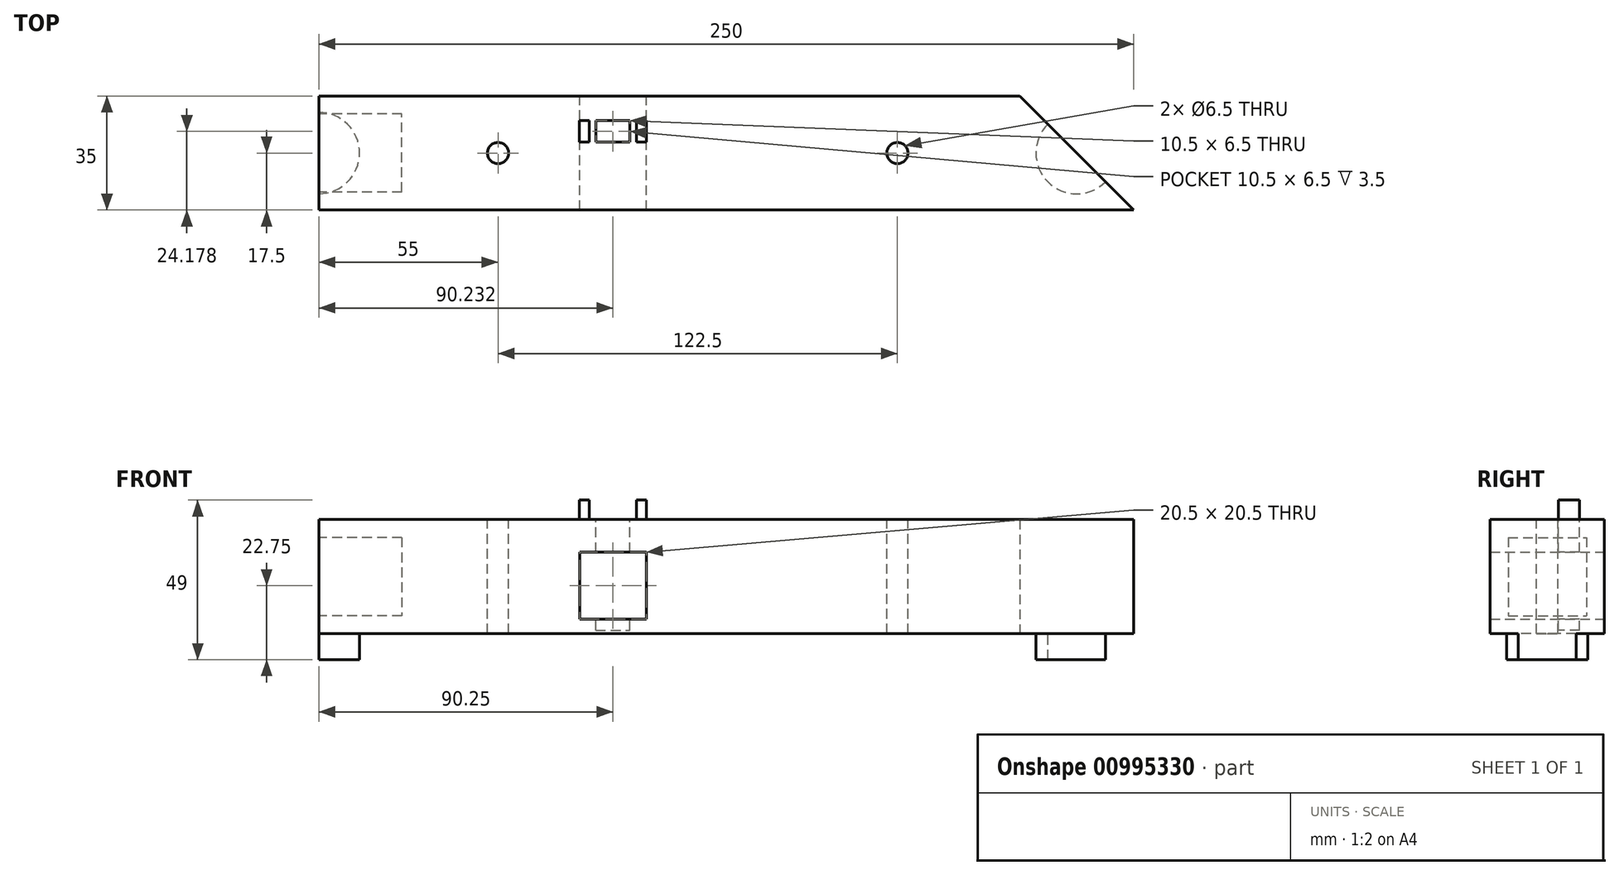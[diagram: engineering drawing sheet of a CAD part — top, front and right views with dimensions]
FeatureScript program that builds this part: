
annotation { "Feature Type Name" : "Feature", "Feature Type Description" : "" }
export const myFeature = defineFeature(function(context is Context, id is Id, definition is map)
    precondition{}
    {
        {
            var Q0;
            Q0=qCreatedBy(makeId("Top.planeOp"),FACE);
            var sketch = newSketch(context, id + "F0", { "sketchPlane" : qUnion([Q0])});
            skLineSegment(sketch, "E0.bottom", {"start": v(125, -17.5) * mm, "end": v(-125, -17.5) * mm});
            skLineSegment(sketch, "E0.top", {"start": v(90, 17.5) * mm, "end": v(-125, 17.5) * mm});
            skLineSegment(sketch, "E0.right", {"start": v(-125, -17.5) * mm, "end": v(-125, 17.5) * mm});
            skPoint(sketch, "E0.middle", {"position": v(0, 0) * mm});
            skPoint(sketch, "E1", {"position": v(90, 17.5) * mm});
            skLineSegment(sketch, "E2", {"start": v(125, -17.5) * mm, "end": v(90, 17.5) * mm});
            skPoint(sketch, "E0.left.end.orphan", {"position": v(125, 17.5) * mm});
            skSolve(sketch);
        }
        {
            var Q0;
            Q0=makeQuery(id+"F0.imprint","IMPRINT",FACE,{"disambiguationData":[TD([[makeQuery(id+"F0.imprint","IMPRINT",EDGE,{"derivedFrom":sQuery(id+"F0.wireOp",EDGE,"E0.bottom")}),-1.0]])]});
            extrude(context, id + "F1", {"entities" : qUnion([Q0]), "depth" : 35 * mm, "offsetDistance" : 25 * mm});
        }
        {
            var Q0;
            Q0=makeQuery(id+"F1.opExtrude","SWEPT_FACE",FACE,{"disambiguationData":[OSD([sQuery(id+"F0.wireOp",EDGE,"E0.right")])]});
            var sketch = newSketch(context, id + "F2", { "sketchPlane" : qUnion([Q0])});
            skLineSegment(sketch, "E3.0", {"start": v(-12, 29.5) * mm, "end": v(-12, 5.5) * mm});
            skLineSegment(sketch, "E3.1", {"start": v(12, 29.5) * mm, "end": v(-12, 29.5) * mm});
            skLineSegment(sketch, "E4.0", {"start": v(12, 5.5) * mm, "end": v(-12, 5.5) * mm});
            skLineSegment(sketch, "E4.1", {"start": v(12, 29.5) * mm, "end": v(12, 5.5) * mm});
            skSolve(sketch);
        }
        {
            var Q0;
            Q0=makeQuery(id+"F2.imprint","IMPRINT",FACE,{"disambiguationData":[TD([[makeQuery(id+"F2.imprint","IMPRINT",EDGE,{"derivedFrom":sQuery(id+"F2.wireOp",EDGE,"E3.0")}),1.0]])]});
            extrude(context, id + "F3", {"entities" : qUnion([Q0]), "operationType" : NewBodyOperationType.REMOVE, "oppositeDirection" : true, "depth" : 25.5 * mm, "offsetDistance" : 25 * mm});
        }
        {
            var Q0;
            Q0=makeQuery(id+"F1.opExtrude","CAP_FACE",FACE,{"disambiguationData":[OSD([sQuery(id+"F0.wireOp",EDGE,"E0.bottom"),sQuery(id+"F0.wireOp",EDGE,"E0.top"),sQuery(id+"F0.wireOp",EDGE,"E0.right"),sQuery(id+"F0.wireOp",EDGE,"E2")])],"isStart":false});
            var sketch = newSketch(context, id + "F4", { "sketchPlane" : qUnion([Q0])});
            skPoint(sketch, "E5", {"position": v(52.5, 0) * mm});
            skPoint(sketch, "E6", {"position": v(107.5, 0) * mm});
            skPoint(sketch, "E7", {"position": v(-125, 0) * mm});
            skPoint(sketch, "E8", {"position": v(-70, 0) * mm});
            skSolve(sketch);
        }
        {
            var Q0;
            Q0=sQuery(id+"F4.wireOp",VERTEX,"E5");
            var Q1;
            Q1=sQuery(id+"F4.wireOp",VERTEX,"E8");
            var Q2;
            Q2=makeQuery(id+"F1.opExtrude","SWEPT_BODY",BODY,{"disambiguationData":[OSD([sQuery(id+"F0.wireOp",EDGE,"E0.bottom"),sQuery(id+"F0.wireOp",EDGE,"E0.top"),sQuery(id+"F0.wireOp",EDGE,"E0.right"),sQuery(id+"F0.wireOp",EDGE,"E2")])]});
            hole(context, id + "F5", {"style" : HoleStyle.SIMPLE, "endStyle" : HoleEndStyle.BLIND, "holeDiameter" : 6.5 * mm, "majorDiameter" : 5 * mm, "holeDepth" : 35 * mm, "isTappedThrough" : true, "tappedDepth" : 12 * mm, "tapClearance" : 3, "locations" : qUnion([Q0, Q1]), "scope" : qUnion([Q2])});
        }
        {
            var Q0;
            Q0=makeQuery(id+"F1.opExtrude","CAP_FACE",FACE,{"disambiguationData":[OSD([sQuery(id+"F0.wireOp",EDGE,"E0.bottom"),sQuery(id+"F0.wireOp",EDGE,"E0.top"),sQuery(id+"F0.wireOp",EDGE,"E0.right"),sQuery(id+"F0.wireOp",EDGE,"E2")])],"isStart":true});
            var sketch = newSketch(context, id + "F6", { "sketchPlane" : qUnion([Q0])});
            skCircle(sketch, "E9", {"center": v(107.5, 0) * mm, "radius": 12.5 * mm});
            skSolve(sketch);
        }
        {
            var Q0;
            {var subQ0=sQuery(id+"F6.wireOp",EDGE,"E9");var subQ1=makeQuery(id+"F1.opExtrude","CAP_EDGE",EDGE,{"disambiguationData":[OSD([sQuery(id+"F0.wireOp",EDGE,"E2")])],"isStart":true});var subQ2=makeQuery(id+"F6.imprint","INTERSECT",VERTEX,{"disambiguationData":[OD(0.0)],"derivedFrom":[subQ1,subQ0]});Q0=makeQuery(id+"F6.imprint","IMPRINT",FACE,{"disambiguationData":[TD([[makeQuery(id+"F6.imprint","IMPRINT",EDGE,{"disambiguationData":[TD([[subQ2,-1.0]])],"derivedFrom":subQ0}),1.0]])]});}
            extrude(context, id + "F7", {"entities" : qUnion([Q0]), "operationType" : NewBodyOperationType.ADD, "depth" : 8 * mm, "offsetDistance" : 25 * mm});
        }
        {
            var Q0;
            Q0=makeQuery(id+"F1.opExtrude","CAP_FACE",FACE,{"disambiguationData":[OSD([sQuery(id+"F0.wireOp",EDGE,"E0.bottom"),sQuery(id+"F0.wireOp",EDGE,"E0.top"),sQuery(id+"F0.wireOp",EDGE,"E0.right"),sQuery(id+"F0.wireOp",EDGE,"E2")])],"isStart":true});
            var sketch = newSketch(context, id + "F8", { "sketchPlane" : qUnion([Q0])});
            skCircle(sketch, "E10", {"center": v(-125, 0) * mm, "radius": 12.5 * mm});
            skSolve(sketch);
        }
        {
            var Q0;
            {var subQ0=sQuery(id+"F8.wireOp",EDGE,"E10");var subQ1=makeQuery(id+"F1.opExtrude","CAP_EDGE",EDGE,{"disambiguationData":[OSD([sQuery(id+"F0.wireOp",EDGE,"E0.right")])],"isStart":true});var subQ2=makeQuery(id+"F8.imprint","INTERSECT",VERTEX,{"disambiguationData":[OD(0.0)],"derivedFrom":[subQ1,subQ0]});Q0=makeQuery(id+"F8.imprint","IMPRINT",FACE,{"disambiguationData":[TD([[makeQuery(id+"F8.imprint","IMPRINT",EDGE,{"disambiguationData":[TD([[subQ2,1.0]])],"derivedFrom":subQ0}),1.0]])]});}
            extrude(context, id + "F9", {"entities" : qUnion([Q0]), "operationType" : NewBodyOperationType.ADD, "depth" : 8 * mm, "offsetDistance" : 25 * mm});
        }
        {
            var Q0;
            Q0=makeQuery(id+"F1.opExtrude","SWEPT_FACE",FACE,{"disambiguationData":[OSD([sQuery(id+"F0.wireOp",EDGE,"E0.top")])]});
            var sketch = newSketch(context, id + "F10", { "sketchPlane" : qUnion([Q0])});
            skPoint(sketch, "E11", {"position": v(45, 25) * mm});
            skLineSegment(sketch, "E12.bottom", {"start": v(45, 25) * mm, "end": v(24.5, 25) * mm});
            skLineSegment(sketch, "E12.top", {"start": v(45, 4.5) * mm, "end": v(24.5, 4.5) * mm});
            skLineSegment(sketch, "E12.left", {"start": v(45, 25) * mm, "end": v(45, 4.5) * mm});
            skLineSegment(sketch, "E12.right", {"start": v(24.5, 25) * mm, "end": v(24.5, 4.5) * mm});
            skSolve(sketch);
        }
        {
            var Q0;
            Q0 = qSketchRegion(id + "F10", true);
            extrude(context, id + "F11", {"entities" : qUnion([Q0]), "operationType" : NewBodyOperationType.REMOVE, "oppositeDirection" : true, "depth" : 100 * mm, "offsetDistance" : 25 * mm});
        }
        {
            var Q0;
            Q0=makeQuery(id+"F1.opExtrude","CAP_FACE",FACE,{"disambiguationData":[OSD([sQuery(id+"F0.wireOp",EDGE,"E0.bottom"),sQuery(id+"F0.wireOp",EDGE,"E0.top"),sQuery(id+"F0.wireOp",EDGE,"E0.right"),sQuery(id+"F0.wireOp",EDGE,"E2")])],"isStart":false});
            var sketch = newSketch(context, id + "F12", { "sketchPlane" : qUnion([Q0])});
            skPoint(sketch, "E13", {"position": v(-40.02, -9.93) * mm});
            skLineSegment(sketch, "E14.bottom", {"start": v(-40.02, -9.93) * mm, "end": v(-29.52, -9.93) * mm});
            skLineSegment(sketch, "E14.top", {"start": v(-40.02, -3.43) * mm, "end": v(-29.52, -3.43) * mm});
            skLineSegment(sketch, "E14.left", {"start": v(-40.02, -9.93) * mm, "end": v(-40.02, -3.43) * mm});
            skLineSegment(sketch, "E14.right", {"start": v(-29.52, -9.93) * mm, "end": v(-29.52, -3.43) * mm});
            skLineSegment(sketch, "E15", {"start": v(-60.73, 0) * mm, "end": v(-19.7, 0) * mm});
            skLineSegment(sketch, "E16.MirrorCS", {"start": v(-40.02, 3.43) * mm, "end": v(-29.52, 3.43) * mm});
            skPoint(sketch, "E17.MirrorP", {"position": v(-40.02, 9.93) * mm});
            skLineSegment(sketch, "E18.MirrorCS", {"start": v(-40.02, 9.93) * mm, "end": v(-40.02, 3.43) * mm});
            skLineSegment(sketch, "E19.MirrorCS", {"start": v(-40.02, 9.93) * mm, "end": v(-29.52, 9.93) * mm});
            skLineSegment(sketch, "E20.MirrorCS", {"start": v(-29.52, 9.93) * mm, "end": v(-29.52, 3.43) * mm});
            skPoint(sketch, "E21", {"position": v(-24.52, 9.93) * mm});
            skPoint(sketch, "E22", {"position": v(-45.02, 9.93) * mm});
            skLineSegment(sketch, "E23.bottom", {"start": v(-24.52, 9.93) * mm, "end": v(-27.52, 9.93) * mm});
            skLineSegment(sketch, "E23.top", {"start": v(-24.52, 3.43) * mm, "end": v(-27.52, 3.43) * mm});
            skLineSegment(sketch, "E23.left", {"start": v(-24.52, 9.93) * mm, "end": v(-24.52, 3.43) * mm});
            skLineSegment(sketch, "E23.right", {"start": v(-27.52, 9.93) * mm, "end": v(-27.52, 3.43) * mm});
            skLineSegment(sketch, "E24.bottom", {"start": v(-45.02, 9.93) * mm, "end": v(-42.02, 9.93) * mm});
            skLineSegment(sketch, "E24.top", {"start": v(-45.02, 3.43) * mm, "end": v(-42.02, 3.43) * mm});
            skLineSegment(sketch, "E24.left", {"start": v(-45.02, 9.93) * mm, "end": v(-45.02, 3.43) * mm});
            skLineSegment(sketch, "E24.right", {"start": v(-42.02, 9.93) * mm, "end": v(-42.02, 3.43) * mm});
            skSolve(sketch);
        }
        {
            var Q0;
            Q0=makeQuery(id+"F12.imprint","IMPRINT",FACE,{"disambiguationData":[TD([[makeQuery(id+"F12.imprint","IMPRINT",EDGE,{"derivedFrom":sQuery(id+"F12.wireOp",EDGE,"E16.MirrorCS")}),1.0]])]});
            extrude(context, id + "F13", {"entities" : qUnion([Q0]), "operationType" : NewBodyOperationType.REMOVE, "oppositeDirection" : true, "depth" : 34 * mm, "offsetDistance" : 25 * mm});
        }
        {
            var Q0;
            Q0=makeQuery(id+"F12.imprint","IMPRINT",FACE,{"disambiguationData":[TD([[makeQuery(id+"F12.imprint","IMPRINT",EDGE,{"derivedFrom":sQuery(id+"F12.wireOp",EDGE,"E24.bottom")}),-1.0]])]});
            var Q1;
            Q1=makeQuery(id+"F12.imprint","IMPRINT",FACE,{"disambiguationData":[TD([[makeQuery(id+"F12.imprint","IMPRINT",EDGE,{"derivedFrom":sQuery(id+"F12.wireOp",EDGE,"E23.bottom")}),1.0]])]});
            extrude(context, id + "F14", {"entities" : qUnion([Q0, Q1]), "operationType" : NewBodyOperationType.ADD, "depth" : 6 * mm, "offsetDistance" : 25 * mm});
        }
    });
